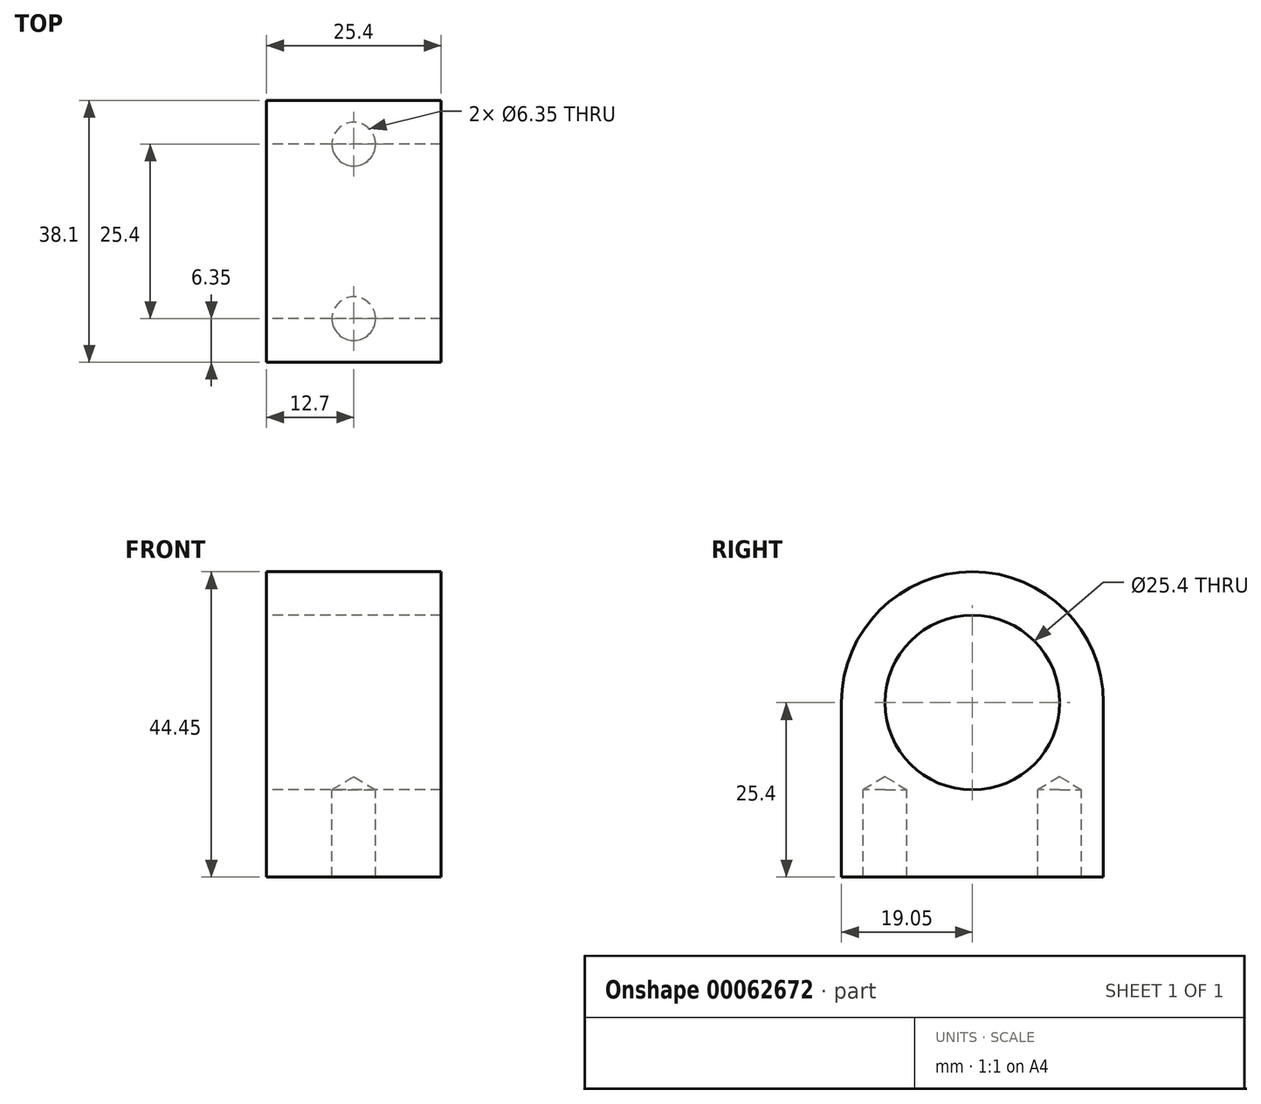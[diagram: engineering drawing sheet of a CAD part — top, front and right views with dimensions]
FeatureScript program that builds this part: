
annotation { "Feature Type Name" : "Feature", "Feature Type Description" : "" }
export const myFeature = defineFeature(function(context is Context, id is Id, definition is map)
    precondition{}
    {
        {
            var Q0;
            Q0=qCreatedBy(makeId("Right.planeOp"),FACE);
            var sketch = newSketch(context, id + "F0", { "sketchPlane" : qUnion([Q0])});
            skLineSegment(sketch, "E0.bottom", {"start": v(-19.05, 0) * mm, "end": v(19.05, 0) * mm});
            skLineSegment(sketch, "E0.top", {"start": v(-19.05, -25.4) * mm, "end": v(19.05, -25.4) * mm});
            skLineSegment(sketch, "E0.left", {"start": v(-19.05, 0) * mm, "end": v(-19.05, -25.4) * mm});
            skLineSegment(sketch, "E0.right", {"start": v(19.05, 0) * mm, "end": v(19.05, -25.4) * mm});
            skArc(sketch, "E1", {"start": v(19.05, 0) * mm, "mid": v(0, 19.05) * mm, "end": v(-19.05, 0) * mm});
            skCircle(sketch, "E2", {"center": v(0, 0) * mm, "radius": 12.7 * mm});
            skSolve(sketch);
        }
        {
            var Q0;
            Q0=makeQuery(id+"F0.imprint","IMPRINT",FACE,{"disambiguationData":[TD([[makeQuery(id+"F0.imprint","IMPRINT",EDGE,{"derivedFrom":sQuery(id+"F0.wireOp",EDGE,"E0.top")}),1.0]])]});
            var Q1;
            {var subQ0=sQuery(id+"F0.wireOp",EDGE,"E1");Q1=makeQuery(id+"F0.imprint","IMPRINT",FACE,{"disambiguationData":[TD([[makeQuery(id+"F0.imprint","IMPRINT",EDGE,{"derivedFrom":subQ0}),1.0]])]});}
            extrude(context, id + "F1", {"entities" : qUnion([Q0, Q1]), "depth" : 25.4 * mm});
        }
        {
            var Q0;
            Q0=makeQuery(id+"F1.opExtrude","SWEPT_FACE",FACE,{"disambiguationData":[OSD([sQuery(id+"F0.wireOp",EDGE,"E0.top")])]});
            var sketch = newSketch(context, id + "F2", { "sketchPlane" : qUnion([Q0])});
            skCircle(sketch, "E3", {"center": v(12.7, 12.7) * mm, "radius": 3.18 * mm});
            skCircle(sketch, "E4", {"center": v(12.7, -12.7) * mm, "radius": 3.18 * mm});
            skSolve(sketch);
        }
        {
            var Q0;
            Q0=sQuery(id+"F2.wireOp",VERTEX,"E3.center");
            var Q1;
            Q1=sQuery(id+"F2.wireOp",VERTEX,"E4.center");
            var Q2;
            Q2=makeQuery(id+"F1.opExtrude","SWEPT_BODY",BODY,{"disambiguationData":[OSD([sQuery(id+"F0.wireOp",EDGE,"E0.top"),sQuery(id+"F0.wireOp",EDGE,"E0.left"),sQuery(id+"F0.wireOp",EDGE,"E0.right"),sQuery(id+"F0.wireOp",EDGE,"E1"),sQuery(id+"F0.wireOp",EDGE,"E2")])]});
            hole(context, id + "F3", {"style" : HoleStyle.SIMPLE, "holeDiameter" : 6.35 * mm, "endStyle" : HoleEndStyle.BLIND, "holeDepth" : 12.7 * mm, "locations" : qUnion([Q0, Q1]), "scope" : qUnion([Q2])});
        }
    });
